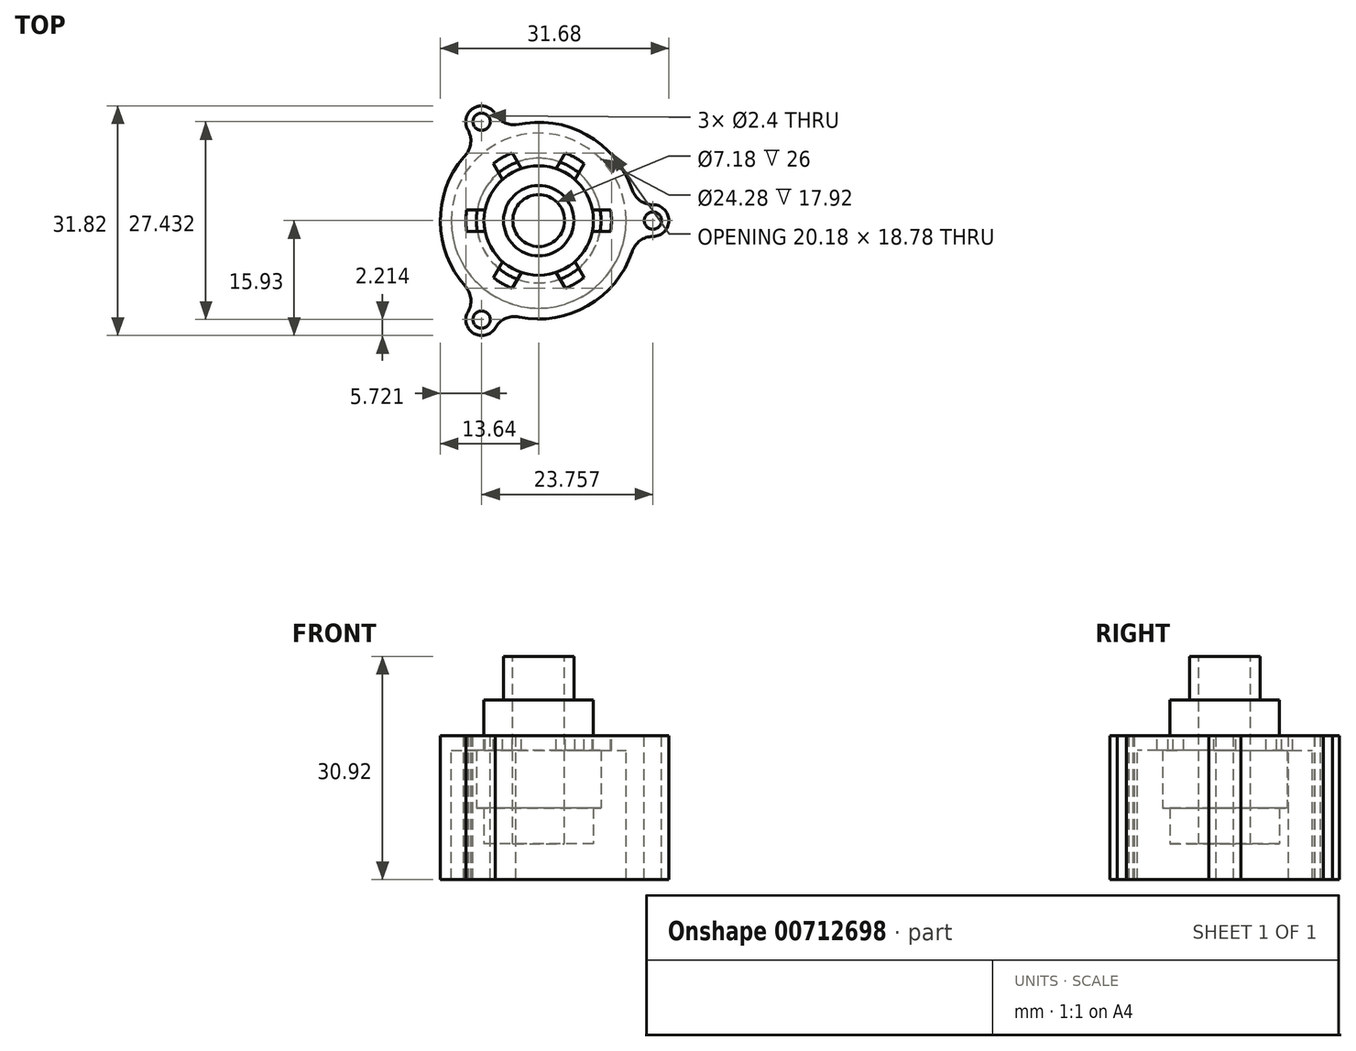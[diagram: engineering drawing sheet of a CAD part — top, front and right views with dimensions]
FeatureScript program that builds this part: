
annotation { "Feature Type Name" : "Feature", "Feature Type Description" : "" }
export const myFeature = defineFeature(function(context is Context, id is Id, definition is map)
    precondition{}
    {
        {
            var Q0;
            Q0=qCreatedBy(makeId("Top.planeOp"),FACE);
            var sketch = newSketch(context, id + "F0", { "sketchPlane" : qUnion([Q0])});
            skCircle(sketch, "E0", {"center": v(0, 0) * mm, "radius": 7.59 * mm});
            skCircle(sketch, "E1", {"center": v(0, 0) * mm, "radius": 1.1 * mm});
            skArc(sketch, "E2", {"start": v(1.75, 0.92) * mm, "mid": v(0.99, 1.71) * mm, "end": v(-0.08, 1.98) * mm});
            skArc(sketch, "E3", {"start": v(3.12, 1.65) * mm, "mid": v(1.76, 3.06) * mm, "end": v(-0.14, 3.53) * mm});
            skArc(sketch, "E4", {"start": v(1.75, 0.92) * mm, "mid": v(2.8, 0.6) * mm, "end": v(3.12, 1.65) * mm});
            skArc(sketch, "E5.MirrorC", {"start": v(1.75, -0.92) * mm, "mid": v(2.8, -0.6) * mm, "end": v(3.12, -1.65) * mm});
            skArc(sketch, "E6.1.0", {"start": v(-1.68, 1.06) * mm, "mid": v(-1.92, 2.12) * mm, "end": v(-2.99, 1.88) * mm});
            skArc(sketch, "E6.2.0", {"start": v(-0.08, -1.98) * mm, "mid": v(-0.88, -2.72) * mm, "end": v(-0.14, -3.53) * mm});
            skArc(sketch, "E7.1.0", {"start": v(-0.08, 1.98) * mm, "mid": v(-0.88, 2.72) * mm, "end": v(-0.14, 3.53) * mm});
            skArc(sketch, "E7.2.0", {"start": v(-1.68, -1.06) * mm, "mid": v(-1.92, -2.12) * mm, "end": v(-2.99, -1.88) * mm});
            skArc(sketch, "E8.trimOffspring", {"start": v(-1.68, 1.06) * mm, "mid": v(-1.98, 0) * mm, "end": v(-1.68, -1.06) * mm});
            skArc(sketch, "E9.trimOffspring", {"start": v(-2.99, 1.88) * mm, "mid": v(-3.53, 0) * mm, "end": v(-2.99, -1.88) * mm});
            skArc(sketch, "E10.trimOffspring", {"start": v(-0.14, -3.53) * mm, "mid": v(1.76, -3.06) * mm, "end": v(3.12, -1.65) * mm});
            skArc(sketch, "E11.trimOffspring", {"start": v(-0.08, -1.98) * mm, "mid": v(0.99, -1.71) * mm, "end": v(1.75, -0.92) * mm});
            skSolve(sketch);
        }
        {
            var Q0;
            Q0=makeQuery(id+"F0.imprint","IMPRINT",FACE,{"disambiguationData":[TD([[makeQuery(id+"F0.imprint","IMPRINT",EDGE,{"derivedFrom":sQuery(id+"F0.wireOp",EDGE,"E0")}),1.0]])]});
            extrude(context, id + "F1", {"entities" : qUnion([Q0]), "depth" : 1.32 * mm, "offsetDistance" : 25 * mm});
        }
        {
            var Q0;
            Q0=makeQuery(id+"F1.opExtrude","CAP_FACE",FACE,{"disambiguationData":[OSD([sQuery(id+"F0.wireOp",EDGE,"E0"),sQuery(id+"F0.wireOp",EDGE,"E1"),sQuery(id+"F0.wireOp",EDGE,"E2"),sQuery(id+"F0.wireOp",EDGE,"E3"),sQuery(id+"F0.wireOp",EDGE,"E4"),sQuery(id+"F0.wireOp",EDGE,"E5.MirrorC"),sQuery(id+"F0.wireOp",EDGE,"E6.1.0"),sQuery(id+"F0.wireOp",EDGE,"E6.2.0"),sQuery(id+"F0.wireOp",EDGE,"E7.1.0"),sQuery(id+"F0.wireOp",EDGE,"E7.2.0"),sQuery(id+"F0.wireOp",EDGE,"E8.trimOffspring"),sQuery(id+"F0.wireOp",EDGE,"E9.trimOffspring"),sQuery(id+"F0.wireOp",EDGE,"E10.trimOffspring"),sQuery(id+"F0.wireOp",EDGE,"E11.trimOffspring")])],"isStart":false});
            var sketch = newSketch(context, id + "F2", { "sketchPlane" : qUnion([Q0])});
            skCircle(sketch, "E12", {"center": v(0, 0) * mm, "radius": 5.59 * mm});
            skCircle(sketch, "E13", {"center": v(0, 0) * mm, "radius": 7.59 * mm});
            skSolve(sketch);
        }
        {
            var Q0;
            Q0 = qSketchRegion(id + "F2", true);
            extrude(context, id + "F3", {"entities" : qUnion([Q0]), "operationType" : NewBodyOperationType.ADD, "depth" : 5 * mm, "offsetDistance" : 25 * mm});
        }
        {
            var Q0;
            Q0=makeQuery(id+"F3.opExtrude","CAP_FACE",FACE,{"disambiguationData":[OSD([sQuery(id+"F2.wireOp",EDGE,"E12"),sQuery(id+"F2.wireOp",EDGE,"E13")])],"isStart":false});
            var sketch = newSketch(context, id + "F4", { "sketchPlane" : qUnion([Q0])});
            skCircle(sketch, "E14", {"center": v(0, 0) * mm, "radius": 5.59 * mm});
            skCircle(sketch, "E15", {"center": v(0, 0) * mm, "radius": 8.64 * mm});
            skSolve(sketch);
        }
        {
            var Q0;
            Q0 = qSketchRegion(id + "F4", true);
            extrude(context, id + "F5", {"entities" : qUnion([Q0]), "operationType" : NewBodyOperationType.ADD, "depth" : 10 * mm, "offsetDistance" : 25 * mm});
        }
        {
            var Q0;
            Q0=makeQuery(id+"F5.opExtrude","CAP_FACE",FACE,{"disambiguationData":[OSD([sQuery(id+"F4.wireOp",EDGE,"E14"),sQuery(id+"F4.wireOp",EDGE,"E15")])],"isStart":false});
            var sketch = newSketch(context, id + "F6", { "sketchPlane" : qUnion([Q0])});
            skArc(sketch, "E16", {"start": v(-10.4, 8.81) * mm, "mid": v(-13.64, -0.19) * mm, "end": v(-10.16, -9.1) * mm});
            skCircle(sketch, "E17", {"center": v(0, 0) * mm, "radius": 3.59 * mm});
            skArc(sketch, "E18", {"start": v(15.84, -2.2) * mm, "mid": v(18.04, 0) * mm, "end": v(15.84, 2.2) * mm});
            skCircle(sketch, "E19", {"center": v(15.84, 0) * mm, "radius": 1.2 * mm});
            skArc(sketch, "E20.1.0", {"start": v(-6.1, 14.92) * mm, "mid": v(-9.16, 15.5) * mm, "end": v(-9.74, 12.45) * mm});
            skArc(sketch, "E20.2.0", {"start": v(-9.85, -12.71) * mm, "mid": v(-9, -15.63) * mm, "end": v(-6.05, -14.93) * mm});
            skPoint(sketch, "E20.center", {"position": v(0, -0.02) * mm});
            skCircle(sketch, "E21.1.0", {"center": v(-7.92, 13.72) * mm, "radius": 1.2 * mm});
            skCircle(sketch, "E21.2.0", {"center": v(-7.92, -13.72) * mm, "radius": 1.2 * mm});
            skArc(sketch, "E22", {"start": v(12.95, 4.29) * mm, "mid": v(14.05, 2.78) * mm, "end": v(15.84, 2.2) * mm});
            skLineSegment(sketch, "E23", {"start": v(15.84, 0) * mm, "end": v(15.84, 2.2) * mm, "construction": true});
            skArc(sketch, "E24.MirrorC", {"start": v(12.95, -4.29) * mm, "mid": v(14.05, -2.78) * mm, "end": v(15.84, -2.2) * mm});
            skArc(sketch, "E25.1.0", {"start": v(-10.4, 8.81) * mm, "mid": v(-9.46, 10.51) * mm, "end": v(-9.74, 12.45) * mm});
            skArc(sketch, "E25.2.0", {"start": v(-2.73, -13.36) * mm, "mid": v(-4.65, -13.59) * mm, "end": v(-6.05, -14.93) * mm});
            skPoint(sketch, "E25.center", {"position": v(0.01, 0) * mm});
            skArc(sketch, "E26.1.0", {"start": v(-3.15, 13.27) * mm, "mid": v(-4.87, 13.65) * mm, "end": v(-6.1, 14.92) * mm});
            skArc(sketch, "E26.2.0", {"start": v(-10.16, -9.1) * mm, "mid": v(-9.4, -10.85) * mm, "end": v(-9.85, -12.71) * mm});
            skArc(sketch, "E27.trimOffspring", {"start": v(-2.73, -13.36) * mm, "mid": v(6.83, -11.8) * mm, "end": v(12.95, -4.29) * mm});
            skArc(sketch, "E28.trimOffspring", {"start": v(12.95, 4.29) * mm, "mid": v(6.65, 11.9) * mm, "end": v(-3.15, 13.27) * mm});
            skSolve(sketch);
        }
        {
            var Q0;
            Q0 = qSketchRegion(id + "F6", true);
            extrude(context, id + "F7", {"entities" : qUnion([Q0]), "operationType" : NewBodyOperationType.ADD, "oppositeDirection" : true, "depth" : 2 * mm, "offsetDistance" : 25 * mm});
        }
        {
            var Q0;
            Q0=makeQuery(id+"F7.opExtrude","CAP_FACE",FACE,{"disambiguationData":[OSD([sQuery(id+"F6.wireOp",EDGE,"E16"),sQuery(id+"F6.wireOp",EDGE,"E17"),sQuery(id+"F6.wireOp",EDGE,"E18"),sQuery(id+"F6.wireOp",EDGE,"E19"),sQuery(id+"F6.wireOp",EDGE,"E20.1.0"),sQuery(id+"F6.wireOp",EDGE,"E20.2.0"),sQuery(id+"F6.wireOp",EDGE,"E21.1.0"),sQuery(id+"F6.wireOp",EDGE,"E21.2.0"),sQuery(id+"F6.wireOp",EDGE,"E22"),sQuery(id+"F6.wireOp",EDGE,"E24.MirrorC"),sQuery(id+"F6.wireOp",EDGE,"E25.1.0"),sQuery(id+"F6.wireOp",EDGE,"E25.2.0"),sQuery(id+"F6.wireOp",EDGE,"E26.1.0"),sQuery(id+"F6.wireOp",EDGE,"E26.2.0"),sQuery(id+"F6.wireOp",EDGE,"E27.trimOffspring"),sQuery(id+"F6.wireOp",EDGE,"E28.trimOffspring")])],"isStart":false});
            var sketch = newSketch(context, id + "F8", { "sketchPlane" : qUnion([Q0])});
            skArc(sketch, "E29.0", {"start": v(-9.85, 12.71) * mm, "mid": v(-9, 15.63) * mm, "end": v(-6.05, 14.93) * mm});
            skArc(sketch, "E29.1", {"start": v(-10.16, 9.1) * mm, "mid": v(-9.4, 10.85) * mm, "end": v(-9.85, 12.71) * mm});
            skArc(sketch, "E29.2", {"start": v(-10.4, -8.81) * mm, "mid": v(-13.64, 0.19) * mm, "end": v(-10.16, 9.1) * mm});
            skArc(sketch, "E29.3", {"start": v(-10.4, -8.81) * mm, "mid": v(-9.46, -10.51) * mm, "end": v(-9.74, -12.45) * mm});
            skArc(sketch, "E29.4", {"start": v(-6.1, -14.92) * mm, "mid": v(-9.16, -15.5) * mm, "end": v(-9.74, -12.45) * mm});
            skArc(sketch, "E29.5", {"start": v(-3.15, -13.27) * mm, "mid": v(-4.87, -13.65) * mm, "end": v(-6.1, -14.92) * mm});
            skArc(sketch, "E29.6", {"start": v(12.95, -4.29) * mm, "mid": v(6.65, -11.9) * mm, "end": v(-3.15, -13.27) * mm});
            skArc(sketch, "E29.7", {"start": v(12.95, -4.29) * mm, "mid": v(14.05, -2.78) * mm, "end": v(15.84, -2.2) * mm});
            skArc(sketch, "E29.8", {"start": v(15.84, 2.2) * mm, "mid": v(18.04, 0) * mm, "end": v(15.84, -2.2) * mm});
            skArc(sketch, "E29.9", {"start": v(12.95, 4.29) * mm, "mid": v(14.05, 2.78) * mm, "end": v(15.84, 2.2) * mm});
            skArc(sketch, "E29.10", {"start": v(-2.73, 13.36) * mm, "mid": v(6.83, 11.8) * mm, "end": v(12.95, 4.29) * mm});
            skArc(sketch, "E29.11", {"start": v(-2.73, 13.36) * mm, "mid": v(-4.65, 13.59) * mm, "end": v(-6.05, 14.93) * mm});
            skCircle(sketch, "E29.12", {"center": v(-7.92, 13.72) * mm, "radius": 1.2 * mm});
            skCircle(sketch, "E29.13", {"center": v(-7.92, -13.72) * mm, "radius": 1.2 * mm});
            skCircle(sketch, "E29.14", {"center": v(15.84, 0) * mm, "radius": 1.2 * mm});
            skCircle(sketch, "E30", {"center": v(0, 0) * mm, "radius": 12.14 * mm});
            skSolve(sketch);
        }
        {
            var Q0;
            Q0 = qSketchRegion(id + "F8", true);
            var Q1;
            Q1=qCreatedBy(makeId("Top.planeOp"),FACE);
            extrude(context, id + "F9", {"entities" : qUnion([Q0]), "operationType" : NewBodyOperationType.ADD, "endBound" : BoundingType.UP_TO_SURFACE, "depth" : 14.5 * mm, "endBoundEntityFace" : qUnion([Q1]), "hasOffset" : true, "offsetDistance" : 3.6 * mm, "offsetOppositeDirection" : true});
        }
        {
            var Q0;
            Q0=makeQuery(id+"F7.boolean.opBoolean","MERGE",FACE,{"derivedFrom":[makeQuery(id+"F5.opExtrude","CAP_FACE",FACE,{"disambiguationData":[OSD([sQuery(id+"F4.wireOp",EDGE,"E14"),sQuery(id+"F4.wireOp",EDGE,"E15")])],"isStart":false}),makeQuery(id+"F7.opExtrude","CAP_FACE",FACE,{"disambiguationData":[OSD([sQuery(id+"F6.wireOp",EDGE,"E16"),sQuery(id+"F6.wireOp",EDGE,"E17"),sQuery(id+"F6.wireOp",EDGE,"E18"),sQuery(id+"F6.wireOp",EDGE,"E19"),sQuery(id+"F6.wireOp",EDGE,"E20.1.0"),sQuery(id+"F6.wireOp",EDGE,"E20.2.0"),sQuery(id+"F6.wireOp",EDGE,"E21.1.0"),sQuery(id+"F6.wireOp",EDGE,"E21.2.0"),sQuery(id+"F6.wireOp",EDGE,"E22"),sQuery(id+"F6.wireOp",EDGE,"E24.MirrorC"),sQuery(id+"F6.wireOp",EDGE,"E25.1.0"),sQuery(id+"F6.wireOp",EDGE,"E25.2.0"),sQuery(id+"F6.wireOp",EDGE,"E26.1.0"),sQuery(id+"F6.wireOp",EDGE,"E26.2.0"),sQuery(id+"F6.wireOp",EDGE,"E27.trimOffspring"),sQuery(id+"F6.wireOp",EDGE,"E28.trimOffspring")])],"isStart":true})]});
            var sketch = newSketch(context, id + "F10", { "sketchPlane" : qUnion([Q0])});
            skCircle(sketch, "E31", {"center": v(0, 0) * mm, "radius": 4.88 * mm});
            skCircle(sketch, "E32.0", {"center": v(0, 0) * mm, "radius": 3.59 * mm});
            skSolve(sketch);
        }
        {
            var Q0;
            Q0 = qSketchRegion(id + "F10", true);
            extrude(context, id + "F11", {"entities" : qUnion([Q0]), "operationType" : NewBodyOperationType.ADD, "depth" : 11 * mm, "offsetDistance" : 25 * mm});
        }
        {
            var Q0;
            Q0=makeQuery(id+"F7.boolean.opBoolean","MERGE",FACE,{"derivedFrom":[makeQuery(id+"F5.opExtrude","CAP_FACE",FACE,{"disambiguationData":[OSD([sQuery(id+"F4.wireOp",EDGE,"E14"),sQuery(id+"F4.wireOp",EDGE,"E15")])],"isStart":false}),makeQuery(id+"F7.opExtrude","CAP_FACE",FACE,{"disambiguationData":[OSD([sQuery(id+"F6.wireOp",EDGE,"E16"),sQuery(id+"F6.wireOp",EDGE,"E17"),sQuery(id+"F6.wireOp",EDGE,"E18"),sQuery(id+"F6.wireOp",EDGE,"E19"),sQuery(id+"F6.wireOp",EDGE,"E20.1.0"),sQuery(id+"F6.wireOp",EDGE,"E20.2.0"),sQuery(id+"F6.wireOp",EDGE,"E21.1.0"),sQuery(id+"F6.wireOp",EDGE,"E21.2.0"),sQuery(id+"F6.wireOp",EDGE,"E22"),sQuery(id+"F6.wireOp",EDGE,"E24.MirrorC"),sQuery(id+"F6.wireOp",EDGE,"E25.1.0"),sQuery(id+"F6.wireOp",EDGE,"E25.2.0"),sQuery(id+"F6.wireOp",EDGE,"E26.1.0"),sQuery(id+"F6.wireOp",EDGE,"E26.2.0"),sQuery(id+"F6.wireOp",EDGE,"E27.trimOffspring"),sQuery(id+"F6.wireOp",EDGE,"E28.trimOffspring")])],"isStart":true})]});
            var sketch = newSketch(context, id + "F12", { "sketchPlane" : qUnion([Q0])});
            skArc(sketch, "E33.0", {"start": v(7.44, -1.5) * mm, "mid": v(7.59, 0) * mm, "end": v(7.44, 1.5) * mm});
            skArc(sketch, "E34", {"start": v(9.98, -1.5) * mm, "mid": v(10.09, 0) * mm, "end": v(9.98, 1.5) * mm});
            skLineSegment(sketch, "E35", {"start": v(7.44, 1.5) * mm, "end": v(9.98, 1.5) * mm});
            skLineSegment(sketch, "E36.MirrorCS", {"start": v(7.44, -1.5) * mm, "end": v(9.98, -1.5) * mm});
            skLineSegment(sketch, "E37.1.0", {"start": v(5.02, 5.7) * mm, "end": v(6.29, 7.89) * mm});
            skArc(sketch, "E37.1.1", {"start": v(6.29, 7.89) * mm, "mid": v(5.04, 8.74) * mm, "end": v(3.69, 9.39) * mm});
            skLineSegment(sketch, "E37.1.2", {"start": v(2.42, 7.2) * mm, "end": v(3.69, 9.39) * mm});
            skArc(sketch, "E37.1.3", {"start": v(5.02, 5.7) * mm, "mid": v(3.8, 6.57) * mm, "end": v(2.42, 7.2) * mm});
            skLineSegment(sketch, "E37.2.0", {"start": v(-2.42, 7.2) * mm, "end": v(-3.69, 9.39) * mm});
            skArc(sketch, "E37.2.1", {"start": v(-3.69, 9.39) * mm, "mid": v(-5.04, 8.74) * mm, "end": v(-6.29, 7.89) * mm});
            skLineSegment(sketch, "E37.2.2", {"start": v(-5.02, 5.7) * mm, "end": v(-6.29, 7.89) * mm});
            skArc(sketch, "E37.2.3", {"start": v(-2.42, 7.2) * mm, "mid": v(-3.8, 6.57) * mm, "end": v(-5.02, 5.7) * mm});
            skLineSegment(sketch, "E37.3.0", {"start": v(-7.44, 1.5) * mm, "end": v(-9.98, 1.5) * mm});
            skArc(sketch, "E37.3.1", {"start": v(-9.98, 1.5) * mm, "mid": v(-10.09, 0) * mm, "end": v(-9.98, -1.5) * mm});
            skLineSegment(sketch, "E37.3.2", {"start": v(-7.44, -1.5) * mm, "end": v(-9.98, -1.5) * mm});
            skArc(sketch, "E37.3.3", {"start": v(-7.44, 1.5) * mm, "mid": v(-7.59, 0) * mm, "end": v(-7.44, -1.5) * mm});
            skLineSegment(sketch, "E37.4.0", {"start": v(-5.02, -5.7) * mm, "end": v(-6.29, -7.89) * mm});
            skArc(sketch, "E37.4.1", {"start": v(-6.29, -7.89) * mm, "mid": v(-5.04, -8.74) * mm, "end": v(-3.69, -9.39) * mm});
            skLineSegment(sketch, "E37.4.2", {"start": v(-2.42, -7.2) * mm, "end": v(-3.69, -9.39) * mm});
            skArc(sketch, "E37.4.3", {"start": v(-5.02, -5.7) * mm, "mid": v(-3.8, -6.57) * mm, "end": v(-2.42, -7.2) * mm});
            skLineSegment(sketch, "E37.5.0", {"start": v(2.42, -7.2) * mm, "end": v(3.69, -9.39) * mm});
            skArc(sketch, "E37.5.1", {"start": v(3.69, -9.39) * mm, "mid": v(5.04, -8.74) * mm, "end": v(6.29, -7.89) * mm});
            skLineSegment(sketch, "E37.5.2", {"start": v(5.02, -5.7) * mm, "end": v(6.29, -7.89) * mm});
            skArc(sketch, "E37.5.3", {"start": v(2.42, -7.2) * mm, "mid": v(3.8, -6.57) * mm, "end": v(5.02, -5.7) * mm});
            skSolve(sketch);
        }
        {
            var Q0;
            Q0 = qSketchRegion(id + "F12", true);
            var Q1;
            {var subQ0=sQuery(id+"F6.wireOp",EDGE,"E22");var subQ1=sQuery(id+"F6.wireOp",EDGE,"E21.1.0");var subQ2=sQuery(id+"F6.wireOp",EDGE,"E20.2.0");var subQ3=sQuery(id+"F6.wireOp",EDGE,"E20.1.0");var subQ4=sQuery(id+"F6.wireOp",EDGE,"E21.2.0");var subQ5=sQuery(id+"F6.wireOp",EDGE,"E25.2.0");var subQ6=sQuery(id+"F6.wireOp",EDGE,"E18");var subQ7=sQuery(id+"F6.wireOp",EDGE,"E24.MirrorC");var subQ8=sQuery(id+"F6.wireOp",EDGE,"E16");var subQ9=sQuery(id+"F6.wireOp",EDGE,"E19");var subQ10=sQuery(id+"F6.wireOp",EDGE,"E25.1.0");var subQ11=sQuery(id+"F6.wireOp",EDGE,"E26.1.0");var subQ12=sQuery(id+"F6.wireOp",EDGE,"E26.2.0");var subQ13=sQuery(id+"F6.wireOp",EDGE,"E27.trimOffspring");var subQ14=sQuery(id+"F6.wireOp",EDGE,"E28.trimOffspring");Q1=makeQuery(id+"F7.boolean.opBoolean","SPLIT",FACE,{"disambiguationData":[TD([makeQuery(id+"F5.opExtrude","SWEPT_FACE",FACE,{"disambiguationData":[OSD([sQuery(id+"F4.wireOp",EDGE,"E15")])]})])],"derivedFrom":makeQuery(id+"F7.opExtrude","CAP_FACE",FACE,{"disambiguationData":[OSD([subQ8,sQuery(id+"F6.wireOp",EDGE,"E17"),subQ6,subQ9,subQ3,subQ2,subQ1,subQ4,subQ0,subQ7,subQ10,subQ5,subQ11,subQ12,subQ13,subQ14])],"isStart":false})});}
            extrude(context, id + "F13", {"entities" : qUnion([Q0]), "operationType" : NewBodyOperationType.REMOVE, "oppositeDirection" : true, "depth" : 2 * mm, "endBoundEntityFace" : qUnion([Q1]), "offsetDistance" : 25 * mm});
        }
        {
            var Q0;
            Q0=makeQuery(id+"F9.opExtrude","CAP_FACE",FACE,{"disambiguationData":[OSD([sQuery(id+"F8.wireOp",EDGE,"E29.0"),sQuery(id+"F8.wireOp",EDGE,"E29.1"),sQuery(id+"F8.wireOp",EDGE,"E29.2"),sQuery(id+"F8.wireOp",EDGE,"E29.3"),sQuery(id+"F8.wireOp",EDGE,"E29.4"),sQuery(id+"F8.wireOp",EDGE,"E29.5"),sQuery(id+"F8.wireOp",EDGE,"E29.6"),sQuery(id+"F8.wireOp",EDGE,"E29.7"),sQuery(id+"F8.wireOp",EDGE,"E29.8"),sQuery(id+"F8.wireOp",EDGE,"E29.9"),sQuery(id+"F8.wireOp",EDGE,"E29.10"),sQuery(id+"F8.wireOp",EDGE,"E29.11"),sQuery(id+"F8.wireOp",EDGE,"E29.12"),sQuery(id+"F8.wireOp",EDGE,"E29.13"),sQuery(id+"F8.wireOp",EDGE,"E29.14"),sQuery(id+"F8.wireOp",EDGE,"E30")])],"isStart":false});
            var sketch = newSketch(context, id + "F14", { "sketchPlane" : qUnion([Q0])});
            skArc(sketch, "E38.0", {"start": v(-12.09, 1.1) * mm, "mid": v(-12.14, 0) * mm, "end": v(-12.09, -1.1) * mm});
            skArc(sketch, "E39", {"start": v(-11.9, -0.84) * mm, "mid": v(-11.26, 0) * mm, "end": v(-11.9, 0.84) * mm});
            skArc(sketch, "E40", {"start": v(-11.9, -0.84) * mm, "mid": v(-12.04, -0.94) * mm, "end": v(-12.09, -1.1) * mm});
            skArc(sketch, "E41.MirrorC", {"start": v(-11.9, 0.84) * mm, "mid": v(-12.04, 0.94) * mm, "end": v(-12.09, 1.1) * mm});
            skArc(sketch, "E42.1.0", {"start": v(-12.04, -1.52) * mm, "mid": v(-11.85, -2.6) * mm, "end": v(-11.57, -3.68) * mm});
            skArc(sketch, "E42.1.1", {"start": v(-11.45, -3.38) * mm, "mid": v(-11, -2.42) * mm, "end": v(-11.8, -1.74) * mm});
            skArc(sketch, "E42.1.2", {"start": v(-11.8, -1.74) * mm, "mid": v(-11.97, -1.67) * mm, "end": v(-12.04, -1.52) * mm});
            skArc(sketch, "E42.1.3", {"start": v(-11.45, -3.38) * mm, "mid": v(-11.56, -3.5) * mm, "end": v(-11.57, -3.68) * mm});
            skArc(sketch, "E42.2.0", {"start": v(-11.44, -4.07) * mm, "mid": v(-11.02, -5.1) * mm, "end": v(-10.5, -6.08) * mm});
            skArc(sketch, "E42.2.1", {"start": v(-10.45, -5.76) * mm, "mid": v(-10.22, -4.73) * mm, "end": v(-11.16, -4.23) * mm});
            skArc(sketch, "E42.2.2", {"start": v(-11.16, -4.23) * mm, "mid": v(-11.33, -4.2) * mm, "end": v(-11.44, -4.07) * mm});
            skArc(sketch, "E42.2.3", {"start": v(-10.45, -5.76) * mm, "mid": v(-10.54, -5.91) * mm, "end": v(-10.5, -6.08) * mm});
            skArc(sketch, "E42.3.0", {"start": v(-10.3, -6.43) * mm, "mid": v(-9.66, -7.35) * mm, "end": v(-8.95, -8.2) * mm});
            skArc(sketch, "E42.3.1", {"start": v(-8.97, -7.88) * mm, "mid": v(-8.97, -6.82) * mm, "end": v(-9.99, -6.53) * mm});
            skArc(sketch, "E42.3.2", {"start": v(-9.99, -6.53) * mm, "mid": v(-10.16, -6.54) * mm, "end": v(-10.3, -6.43) * mm});
            skArc(sketch, "E42.3.3", {"start": v(-8.97, -7.88) * mm, "mid": v(-9.02, -8.04) * mm, "end": v(-8.95, -8.2) * mm});
            skArc(sketch, "E42.4.0", {"start": v(-8.67, -8.5) * mm, "mid": v(-7.86, -9.25) * mm, "end": v(-6.98, -9.93) * mm});
            skArc(sketch, "E42.4.1", {"start": v(-7.06, -9.62) * mm, "mid": v(-7.3, -8.58) * mm, "end": v(-8.35, -8.53) * mm});
            skArc(sketch, "E42.4.2", {"start": v(-8.35, -8.53) * mm, "mid": v(-8.52, -8.57) * mm, "end": v(-8.67, -8.5) * mm});
            skArc(sketch, "E42.4.3", {"start": v(-7.06, -9.62) * mm, "mid": v(-7.08, -9.79) * mm, "end": v(-6.98, -9.93) * mm});
            skArc(sketch, "E42.5.0", {"start": v(-6.64, -10.16) * mm, "mid": v(-5.69, -10.72) * mm, "end": v(-4.68, -11.2) * mm});
            skArc(sketch, "E42.5.1", {"start": v(-4.83, -10.91) * mm, "mid": v(-5.28, -9.95) * mm, "end": v(-6.32, -10.12) * mm});
            skArc(sketch, "E42.5.2", {"start": v(-6.32, -10.12) * mm, "mid": v(-6.47, -10.2) * mm, "end": v(-6.64, -10.16) * mm});
            skArc(sketch, "E42.5.3", {"start": v(-4.83, -10.91) * mm, "mid": v(-4.8, -11.08) * mm, "end": v(-4.68, -11.2) * mm});
            skArc(sketch, "E42.6.0", {"start": v(-4.3, -11.35) * mm, "mid": v(-3.25, -11.7) * mm, "end": v(-2.17, -11.94) * mm});
            skArc(sketch, "E42.6.1", {"start": v(-2.37, -11.7) * mm, "mid": v(-3.01, -10.85) * mm, "end": v(-4, -11.25) * mm});
            skArc(sketch, "E42.6.2", {"start": v(-4, -11.25) * mm, "mid": v(-4.13, -11.35) * mm, "end": v(-4.3, -11.35) * mm});
            skArc(sketch, "E42.6.3", {"start": v(-2.37, -11.7) * mm, "mid": v(-2.31, -11.86) * mm, "end": v(-2.17, -11.94) * mm});
            skArc(sketch, "E42.7.0", {"start": v(-1.76, -12) * mm, "mid": v(-0.66, -12.12) * mm, "end": v(0.45, -12.13) * mm});
            skArc(sketch, "E42.7.1", {"start": v(0.2, -11.93) * mm, "mid": v(-0.6, -11.25) * mm, "end": v(-1.49, -11.84) * mm});
            skArc(sketch, "E42.7.2", {"start": v(-1.49, -11.84) * mm, "mid": v(-1.6, -11.98) * mm, "end": v(-1.76, -12) * mm});
            skArc(sketch, "E42.7.3", {"start": v(0.2, -11.93) * mm, "mid": v(0.29, -12.08) * mm, "end": v(0.45, -12.13) * mm});
            skArc(sketch, "E42.8.0", {"start": v(0.86, -12.1) * mm, "mid": v(1.96, -11.98) * mm, "end": v(3.05, -11.75) * mm});
            skArc(sketch, "E42.8.1", {"start": v(2.76, -11.61) * mm, "mid": v(1.82, -11.11) * mm, "end": v(1.1, -11.88) * mm});
            skArc(sketch, "E42.8.2", {"start": v(1.1, -11.88) * mm, "mid": v(1.02, -12.04) * mm, "end": v(0.86, -12.1) * mm});
            skArc(sketch, "E42.8.3", {"start": v(2.76, -11.61) * mm, "mid": v(2.88, -11.73) * mm, "end": v(3.05, -11.75) * mm});
            skArc(sketch, "E42.9.0", {"start": v(3.45, -11.64) * mm, "mid": v(4.5, -11.28) * mm, "end": v(5.5, -10.82) * mm});
            skArc(sketch, "E42.9.1", {"start": v(5.2, -10.75) * mm, "mid": v(4.17, -10.46) * mm, "end": v(3.62, -11.37) * mm});
            skArc(sketch, "E42.9.2", {"start": v(3.62, -11.37) * mm, "mid": v(3.58, -11.54) * mm, "end": v(3.45, -11.64) * mm});
            skArc(sketch, "E42.9.3", {"start": v(5.2, -10.75) * mm, "mid": v(5.33, -10.84) * mm, "end": v(5.5, -10.82) * mm});
            skArc(sketch, "E42.10.0", {"start": v(5.87, -10.63) * mm, "mid": v(6.81, -10.05) * mm, "end": v(7.7, -9.38) * mm});
            skArc(sketch, "E42.10.1", {"start": v(7.38, -9.38) * mm, "mid": v(6.32, -9.32) * mm, "end": v(5.98, -10.33) * mm});
            skArc(sketch, "E42.10.2", {"start": v(5.98, -10.33) * mm, "mid": v(5.98, -10.5) * mm, "end": v(5.87, -10.63) * mm});
            skArc(sketch, "E42.10.3", {"start": v(7.38, -9.38) * mm, "mid": v(7.54, -9.44) * mm, "end": v(7.7, -9.38) * mm});
            skArc(sketch, "E42.11.0", {"start": v(8.01, -9.12) * mm, "mid": v(8.81, -8.35) * mm, "end": v(9.54, -7.5) * mm});
            skArc(sketch, "E42.11.1", {"start": v(9.22, -7.57) * mm, "mid": v(8.18, -7.75) * mm, "end": v(8.06, -8.8) * mm});
            skArc(sketch, "E42.11.2", {"start": v(8.06, -8.8) * mm, "mid": v(8.1, -8.97) * mm, "end": v(8.01, -9.12) * mm});
            skArc(sketch, "E42.11.3", {"start": v(9.22, -7.57) * mm, "mid": v(9.4, -7.6) * mm, "end": v(9.54, -7.5) * mm});
            skArc(sketch, "E42.12.0", {"start": v(9.79, -7.18) * mm, "mid": v(10.4, -6.26) * mm, "end": v(10.93, -5.28) * mm});
            skArc(sketch, "E42.12.1", {"start": v(10.64, -5.41) * mm, "mid": v(9.65, -5.8) * mm, "end": v(9.77, -6.86) * mm});
            skArc(sketch, "E42.12.2", {"start": v(9.77, -6.86) * mm, "mid": v(9.83, -7.02) * mm, "end": v(9.79, -7.18) * mm});
            skArc(sketch, "E42.12.3", {"start": v(10.64, -5.41) * mm, "mid": v(10.8, -5.4) * mm, "end": v(10.93, -5.28) * mm});
            skArc(sketch, "E42.13.0", {"start": v(11.1, -4.9) * mm, "mid": v(11.5, -3.88) * mm, "end": v(11.8, -2.81) * mm});
            skArc(sketch, "E42.13.1", {"start": v(11.55, -3) * mm, "mid": v(10.67, -3.6) * mm, "end": v(11.01, -4.6) * mm});
            skArc(sketch, "E42.13.2", {"start": v(11.01, -4.6) * mm, "mid": v(11.11, -4.74) * mm, "end": v(11.1, -4.9) * mm});
            skArc(sketch, "E42.13.3", {"start": v(11.55, -3) * mm, "mid": v(11.71, -2.95) * mm, "end": v(11.8, -2.81) * mm});
            skArc(sketch, "E42.14.0", {"start": v(11.9, -2.4) * mm, "mid": v(12.07, -1.31) * mm, "end": v(12.14, -0.2) * mm});
            skArc(sketch, "E42.14.1", {"start": v(11.93, -0.45) * mm, "mid": v(11.2, -1.22) * mm, "end": v(11.74, -2.13) * mm});
            skArc(sketch, "E42.14.2", {"start": v(11.74, -2.13) * mm, "mid": v(11.87, -2.24) * mm, "end": v(11.9, -2.4) * mm});
            skArc(sketch, "E42.14.3", {"start": v(11.93, -0.45) * mm, "mid": v(12.08, -0.37) * mm, "end": v(12.14, -0.2) * mm});
            skArc(sketch, "E42.15.0", {"start": v(12.14, 0.2) * mm, "mid": v(12.07, 1.31) * mm, "end": v(11.9, 2.4) * mm});
            skArc(sketch, "E42.15.1", {"start": v(11.74, 2.13) * mm, "mid": v(11.2, 1.22) * mm, "end": v(11.93, 0.45) * mm});
            skArc(sketch, "E42.15.2", {"start": v(11.93, 0.45) * mm, "mid": v(12.08, 0.37) * mm, "end": v(12.14, 0.2) * mm});
            skArc(sketch, "E42.15.3", {"start": v(11.74, 2.13) * mm, "mid": v(11.87, 2.24) * mm, "end": v(11.9, 2.4) * mm});
            skArc(sketch, "E42.16.0", {"start": v(11.8, 2.81) * mm, "mid": v(11.5, 3.88) * mm, "end": v(11.1, 4.9) * mm});
            skArc(sketch, "E42.16.1", {"start": v(11.01, 4.6) * mm, "mid": v(10.67, 3.6) * mm, "end": v(11.55, 3) * mm});
            skArc(sketch, "E42.16.2", {"start": v(11.55, 3) * mm, "mid": v(11.71, 2.95) * mm, "end": v(11.8, 2.81) * mm});
            skArc(sketch, "E42.16.3", {"start": v(11.01, 4.6) * mm, "mid": v(11.11, 4.74) * mm, "end": v(11.1, 4.9) * mm});
            skArc(sketch, "E42.17.0", {"start": v(10.93, 5.28) * mm, "mid": v(10.4, 6.26) * mm, "end": v(9.79, 7.18) * mm});
            skArc(sketch, "E42.17.1", {"start": v(9.77, 6.86) * mm, "mid": v(9.65, 5.8) * mm, "end": v(10.64, 5.41) * mm});
            skArc(sketch, "E42.17.2", {"start": v(10.64, 5.41) * mm, "mid": v(10.8, 5.4) * mm, "end": v(10.93, 5.28) * mm});
            skArc(sketch, "E42.17.3", {"start": v(9.77, 6.86) * mm, "mid": v(9.83, 7.02) * mm, "end": v(9.79, 7.18) * mm});
            skArc(sketch, "E42.18.0", {"start": v(9.54, 7.5) * mm, "mid": v(8.81, 8.35) * mm, "end": v(8.01, 9.12) * mm});
            skArc(sketch, "E42.18.1", {"start": v(8.06, 8.8) * mm, "mid": v(8.18, 7.75) * mm, "end": v(9.22, 7.57) * mm});
            skArc(sketch, "E42.18.2", {"start": v(9.22, 7.57) * mm, "mid": v(9.4, 7.6) * mm, "end": v(9.54, 7.5) * mm});
            skArc(sketch, "E42.18.3", {"start": v(8.06, 8.8) * mm, "mid": v(8.1, 8.97) * mm, "end": v(8.01, 9.12) * mm});
            skArc(sketch, "E42.19.0", {"start": v(7.7, 9.38) * mm, "mid": v(6.81, 10.05) * mm, "end": v(5.87, 10.63) * mm});
            skArc(sketch, "E42.19.1", {"start": v(5.98, 10.33) * mm, "mid": v(6.32, 9.32) * mm, "end": v(7.38, 9.38) * mm});
            skArc(sketch, "E42.19.2", {"start": v(7.38, 9.38) * mm, "mid": v(7.54, 9.44) * mm, "end": v(7.7, 9.38) * mm});
            skArc(sketch, "E42.19.3", {"start": v(5.98, 10.33) * mm, "mid": v(5.98, 10.5) * mm, "end": v(5.87, 10.63) * mm});
            skArc(sketch, "E42.20.0", {"start": v(5.5, 10.82) * mm, "mid": v(4.5, 11.28) * mm, "end": v(3.45, 11.64) * mm});
            skArc(sketch, "E42.20.1", {"start": v(3.62, 11.37) * mm, "mid": v(4.17, 10.46) * mm, "end": v(5.2, 10.75) * mm});
            skArc(sketch, "E42.20.2", {"start": v(5.2, 10.75) * mm, "mid": v(5.33, 10.84) * mm, "end": v(5.5, 10.82) * mm});
            skArc(sketch, "E42.20.3", {"start": v(3.62, 11.37) * mm, "mid": v(3.58, 11.54) * mm, "end": v(3.45, 11.64) * mm});
            skArc(sketch, "E42.21.0", {"start": v(3.05, 11.75) * mm, "mid": v(1.96, 11.98) * mm, "end": v(0.86, 12.1) * mm});
            skArc(sketch, "E42.21.1", {"start": v(1.1, 11.88) * mm, "mid": v(1.82, 11.11) * mm, "end": v(2.76, 11.61) * mm});
            skArc(sketch, "E42.21.2", {"start": v(2.76, 11.61) * mm, "mid": v(2.88, 11.73) * mm, "end": v(3.05, 11.75) * mm});
            skArc(sketch, "E42.21.3", {"start": v(1.1, 11.88) * mm, "mid": v(1.02, 12.04) * mm, "end": v(0.86, 12.1) * mm});
            skArc(sketch, "E42.22.0", {"start": v(0.45, 12.13) * mm, "mid": v(-0.66, 12.12) * mm, "end": v(-1.76, 12) * mm});
            skArc(sketch, "E42.22.1", {"start": v(-1.49, 11.84) * mm, "mid": v(-0.6, 11.25) * mm, "end": v(0.2, 11.93) * mm});
            skArc(sketch, "E42.22.2", {"start": v(0.2, 11.93) * mm, "mid": v(0.29, 12.08) * mm, "end": v(0.45, 12.13) * mm});
            skArc(sketch, "E42.22.3", {"start": v(-1.49, 11.84) * mm, "mid": v(-1.6, 11.98) * mm, "end": v(-1.76, 12) * mm});
            skArc(sketch, "E42.23.0", {"start": v(-2.17, 11.94) * mm, "mid": v(-3.25, 11.7) * mm, "end": v(-4.3, 11.35) * mm});
            skArc(sketch, "E42.23.1", {"start": v(-4, 11.25) * mm, "mid": v(-3.01, 10.85) * mm, "end": v(-2.37, 11.7) * mm});
            skArc(sketch, "E42.23.2", {"start": v(-2.37, 11.7) * mm, "mid": v(-2.31, 11.86) * mm, "end": v(-2.17, 11.94) * mm});
            skArc(sketch, "E42.23.3", {"start": v(-4, 11.25) * mm, "mid": v(-4.13, 11.35) * mm, "end": v(-4.3, 11.35) * mm});
            skArc(sketch, "E42.24.0", {"start": v(-4.68, 11.2) * mm, "mid": v(-5.69, 10.72) * mm, "end": v(-6.64, 10.16) * mm});
            skArc(sketch, "E42.24.1", {"start": v(-6.32, 10.12) * mm, "mid": v(-5.28, 9.95) * mm, "end": v(-4.83, 10.91) * mm});
            skArc(sketch, "E42.24.2", {"start": v(-4.83, 10.91) * mm, "mid": v(-4.8, 11.08) * mm, "end": v(-4.68, 11.2) * mm});
            skArc(sketch, "E42.24.3", {"start": v(-6.32, 10.12) * mm, "mid": v(-6.47, 10.2) * mm, "end": v(-6.64, 10.16) * mm});
            skArc(sketch, "E42.25.0", {"start": v(-6.98, 9.93) * mm, "mid": v(-7.86, 9.25) * mm, "end": v(-8.67, 8.5) * mm});
            skArc(sketch, "E42.25.1", {"start": v(-8.35, 8.53) * mm, "mid": v(-7.3, 8.58) * mm, "end": v(-7.06, 9.62) * mm});
            skArc(sketch, "E42.25.2", {"start": v(-7.06, 9.62) * mm, "mid": v(-7.08, 9.79) * mm, "end": v(-6.98, 9.93) * mm});
            skArc(sketch, "E42.25.3", {"start": v(-8.35, 8.53) * mm, "mid": v(-8.52, 8.57) * mm, "end": v(-8.67, 8.5) * mm});
            skArc(sketch, "E42.26.0", {"start": v(-8.95, 8.2) * mm, "mid": v(-9.66, 7.35) * mm, "end": v(-10.3, 6.43) * mm});
            skArc(sketch, "E42.26.1", {"start": v(-9.99, 6.53) * mm, "mid": v(-8.97, 6.82) * mm, "end": v(-8.97, 7.88) * mm});
            skArc(sketch, "E42.26.2", {"start": v(-8.97, 7.88) * mm, "mid": v(-9.02, 8.04) * mm, "end": v(-8.95, 8.2) * mm});
            skArc(sketch, "E42.26.3", {"start": v(-9.99, 6.53) * mm, "mid": v(-10.16, 6.54) * mm, "end": v(-10.3, 6.43) * mm});
            skArc(sketch, "E42.27.0", {"start": v(-10.5, 6.08) * mm, "mid": v(-11.02, 5.1) * mm, "end": v(-11.44, 4.07) * mm});
            skArc(sketch, "E42.27.1", {"start": v(-11.16, 4.23) * mm, "mid": v(-10.22, 4.73) * mm, "end": v(-10.45, 5.76) * mm});
            skArc(sketch, "E42.27.2", {"start": v(-10.45, 5.76) * mm, "mid": v(-10.54, 5.91) * mm, "end": v(-10.5, 6.08) * mm});
            skArc(sketch, "E42.27.3", {"start": v(-11.16, 4.23) * mm, "mid": v(-11.33, 4.2) * mm, "end": v(-11.44, 4.07) * mm});
            skArc(sketch, "E42.28.0", {"start": v(-11.57, 3.68) * mm, "mid": v(-11.85, 2.6) * mm, "end": v(-12.04, 1.52) * mm});
            skArc(sketch, "E42.28.1", {"start": v(-11.8, 1.74) * mm, "mid": v(-11, 2.42) * mm, "end": v(-11.45, 3.38) * mm});
            skArc(sketch, "E42.28.2", {"start": v(-11.45, 3.38) * mm, "mid": v(-11.56, 3.5) * mm, "end": v(-11.57, 3.68) * mm});
            skArc(sketch, "E42.28.3", {"start": v(-11.8, 1.74) * mm, "mid": v(-11.97, 1.67) * mm, "end": v(-12.04, 1.52) * mm});
            skSolve(sketch);
        }
        {
            var Q0;
            Q0=makeQuery(id+"F7.boolean.opBoolean","MERGE",FACE,{"derivedFrom":[makeQuery(id+"F5.opExtrude","CAP_FACE",FACE,{"disambiguationData":[OSD([sQuery(id+"F4.wireOp",EDGE,"E14"),sQuery(id+"F4.wireOp",EDGE,"E15")])],"isStart":false}),makeQuery(id+"F7.opExtrude","CAP_FACE",FACE,{"disambiguationData":[OSD([sQuery(id+"F6.wireOp",EDGE,"E16"),sQuery(id+"F6.wireOp",EDGE,"E17"),sQuery(id+"F6.wireOp",EDGE,"E18"),sQuery(id+"F6.wireOp",EDGE,"E19"),sQuery(id+"F6.wireOp",EDGE,"E20.1.0"),sQuery(id+"F6.wireOp",EDGE,"E20.2.0"),sQuery(id+"F6.wireOp",EDGE,"E21.1.0"),sQuery(id+"F6.wireOp",EDGE,"E21.2.0"),sQuery(id+"F6.wireOp",EDGE,"E22"),sQuery(id+"F6.wireOp",EDGE,"E24.MirrorC"),sQuery(id+"F6.wireOp",EDGE,"E25.1.0"),sQuery(id+"F6.wireOp",EDGE,"E25.2.0"),sQuery(id+"F6.wireOp",EDGE,"E26.1.0"),sQuery(id+"F6.wireOp",EDGE,"E26.2.0"),sQuery(id+"F6.wireOp",EDGE,"E27.trimOffspring"),sQuery(id+"F6.wireOp",EDGE,"E28.trimOffspring")])],"isStart":true})]});
            var sketch = newSketch(context, id + "F15", { "sketchPlane" : qUnion([Q0])});
            skCircle(sketch, "E43.0", {"center": v(0, 0) * mm, "radius": 4.88 * mm});
            skCircle(sketch, "E44", {"center": v(0, 0) * mm, "radius": 7.59 * mm});
            skSolve(sketch);
        }
        {
            var Q0;
            Q0 = qSketchRegion(id + "F15", true);
            extrude(context, id + "F16", {"entities" : qUnion([Q0]), "operationType" : NewBodyOperationType.ADD, "depth" : 5 * mm, "offsetDistance" : 25 * mm});
        }
        {
            var Q0;
            Q0=makeQuery(id+"F1.opExtrude","CAP_FACE",FACE,{"disambiguationData":[OSD([sQuery(id+"F0.wireOp",EDGE,"E0"),sQuery(id+"F0.wireOp",EDGE,"E1"),sQuery(id+"F0.wireOp",EDGE,"E2"),sQuery(id+"F0.wireOp",EDGE,"E3"),sQuery(id+"F0.wireOp",EDGE,"E4"),sQuery(id+"F0.wireOp",EDGE,"E5.MirrorC"),sQuery(id+"F0.wireOp",EDGE,"E6.1.0"),sQuery(id+"F0.wireOp",EDGE,"E6.2.0"),sQuery(id+"F0.wireOp",EDGE,"E7.1.0"),sQuery(id+"F0.wireOp",EDGE,"E7.2.0"),sQuery(id+"F0.wireOp",EDGE,"E8.trimOffspring"),sQuery(id+"F0.wireOp",EDGE,"E9.trimOffspring"),sQuery(id+"F0.wireOp",EDGE,"E10.trimOffspring"),sQuery(id+"F0.wireOp",EDGE,"E11.trimOffspring")])],"isStart":false});
            var sketch = newSketch(context, id + "F17", { "sketchPlane" : qUnion([Q0])});
            skCircle(sketch, "E45.0", {"center": v(0, 0) * mm, "radius": 5.59 * mm});
            skCircle(sketch, "E46.0", {"center": v(0, 0) * mm, "radius": 3.59 * mm});
            skSolve(sketch);
        }
        {
            var Q0;
            Q0 = qSketchRegion(id + "F17", true);
            var Q1;
            {var subQ0=sQuery(id+"F6.wireOp",EDGE,"E17");Q1=makeQuery(id+"F7.boolean.opBoolean","SPLIT",FACE,{"disambiguationData":[TD([makeQuery(id+"F3.opExtrude","SWEPT_FACE",FACE,{"disambiguationData":[OSD([sQuery(id+"F2.wireOp",EDGE,"E12")])]})])],"derivedFrom":makeQuery(id+"F7.opExtrude","CAP_FACE",FACE,{"disambiguationData":[OSD([sQuery(id+"F6.wireOp",EDGE,"E16"),subQ0,sQuery(id+"F6.wireOp",EDGE,"E18"),sQuery(id+"F6.wireOp",EDGE,"E19"),sQuery(id+"F6.wireOp",EDGE,"E20.1.0"),sQuery(id+"F6.wireOp",EDGE,"E20.2.0"),sQuery(id+"F6.wireOp",EDGE,"E21.1.0"),sQuery(id+"F6.wireOp",EDGE,"E21.2.0"),sQuery(id+"F6.wireOp",EDGE,"E22"),sQuery(id+"F6.wireOp",EDGE,"E24.MirrorC"),sQuery(id+"F6.wireOp",EDGE,"E25.1.0"),sQuery(id+"F6.wireOp",EDGE,"E25.2.0"),sQuery(id+"F6.wireOp",EDGE,"E26.1.0"),sQuery(id+"F6.wireOp",EDGE,"E26.2.0"),sQuery(id+"F6.wireOp",EDGE,"E27.trimOffspring"),sQuery(id+"F6.wireOp",EDGE,"E28.trimOffspring")])],"isStart":false})});}
            extrude(context, id + "F18", {"entities" : qUnion([Q0]), "operationType" : NewBodyOperationType.ADD, "endBound" : BoundingType.UP_TO_SURFACE, "depth" : 25 * mm, "endBoundEntityFace" : qUnion([Q1]), "offsetDistance" : 25 * mm});
        }
        {
            var Q0;
            Q0=makeQuery(id+"F1.opExtrude","CAP_FACE",FACE,{"disambiguationData":[OSD([sQuery(id+"F0.wireOp",EDGE,"E0"),sQuery(id+"F0.wireOp",EDGE,"E1"),sQuery(id+"F0.wireOp",EDGE,"E2"),sQuery(id+"F0.wireOp",EDGE,"E3"),sQuery(id+"F0.wireOp",EDGE,"E4"),sQuery(id+"F0.wireOp",EDGE,"E5.MirrorC"),sQuery(id+"F0.wireOp",EDGE,"E6.1.0"),sQuery(id+"F0.wireOp",EDGE,"E6.2.0"),sQuery(id+"F0.wireOp",EDGE,"E7.1.0"),sQuery(id+"F0.wireOp",EDGE,"E7.2.0"),sQuery(id+"F0.wireOp",EDGE,"E8.trimOffspring"),sQuery(id+"F0.wireOp",EDGE,"E9.trimOffspring"),sQuery(id+"F0.wireOp",EDGE,"E10.trimOffspring"),sQuery(id+"F0.wireOp",EDGE,"E11.trimOffspring")])],"isStart":true});
            var sketch = newSketch(context, id + "F19", { "sketchPlane" : qUnion([Q0])});
            skCircle(sketch, "E47.0", {"center": v(0, 0) * mm, "radius": 7.59 * mm});
            skSolve(sketch);
        }
        {
            var Q0;
            Q0 = qSketchRegion(id + "F19", true);
            extrude(context, id + "F20", {"entities" : qUnion([Q0]), "operationType" : NewBodyOperationType.REMOVE, "oppositeDirection" : true, "depth" : 1.32 * mm, "offsetDistance" : 25 * mm});
        }
    });
